# Revit family: Bodensteckdose UDHOME2, mit Tubus für nass gepflegte Fußböden
name_source: partatom
category: Generic Models
revit_build: Autodesk Revit 2015 (Build: 20140606_1530(x64)
units: mm (PartAtom-declared; Revit-internal decimal feet)

## types (2) — shared parameters
Height = 115 mm  [stored 0.377297 ft]
Height 1 = 108 mm  [stored 0.354331 ft]
HeightCalc = 115 mm  [stored 0.377297 ft]
Length = 140 mm  [stored 0.459318 ft]
Length 1 = 138 mm  [stored 0.452756 ft]
Manufacturer = OBO Bettermann
Material = Aluminum
URL = http://www.obo-bettermann.com
Width = 140 mm  [stored 0.459318 ft]
Width 1 = 138 mm  [stored 0.452756 ft]

## per-type parameters (varying)
| type | GTIN | Manufacturer Art.No. |
| UDHOME2 AF | 4012196266746 | 7427091 |
| UDHOME2 AF V | 4012195842767 | 7368396 |

note: column(s) folded — value = type name in every type: Article Type

note: [stored X ft] marks values corroborated as IEEE doubles in the binary element streams (Revit-internal decimal feet)

## geometry (parser evidence)
native form markers: Sweep x2
no freeform markers — native parametric forms only
